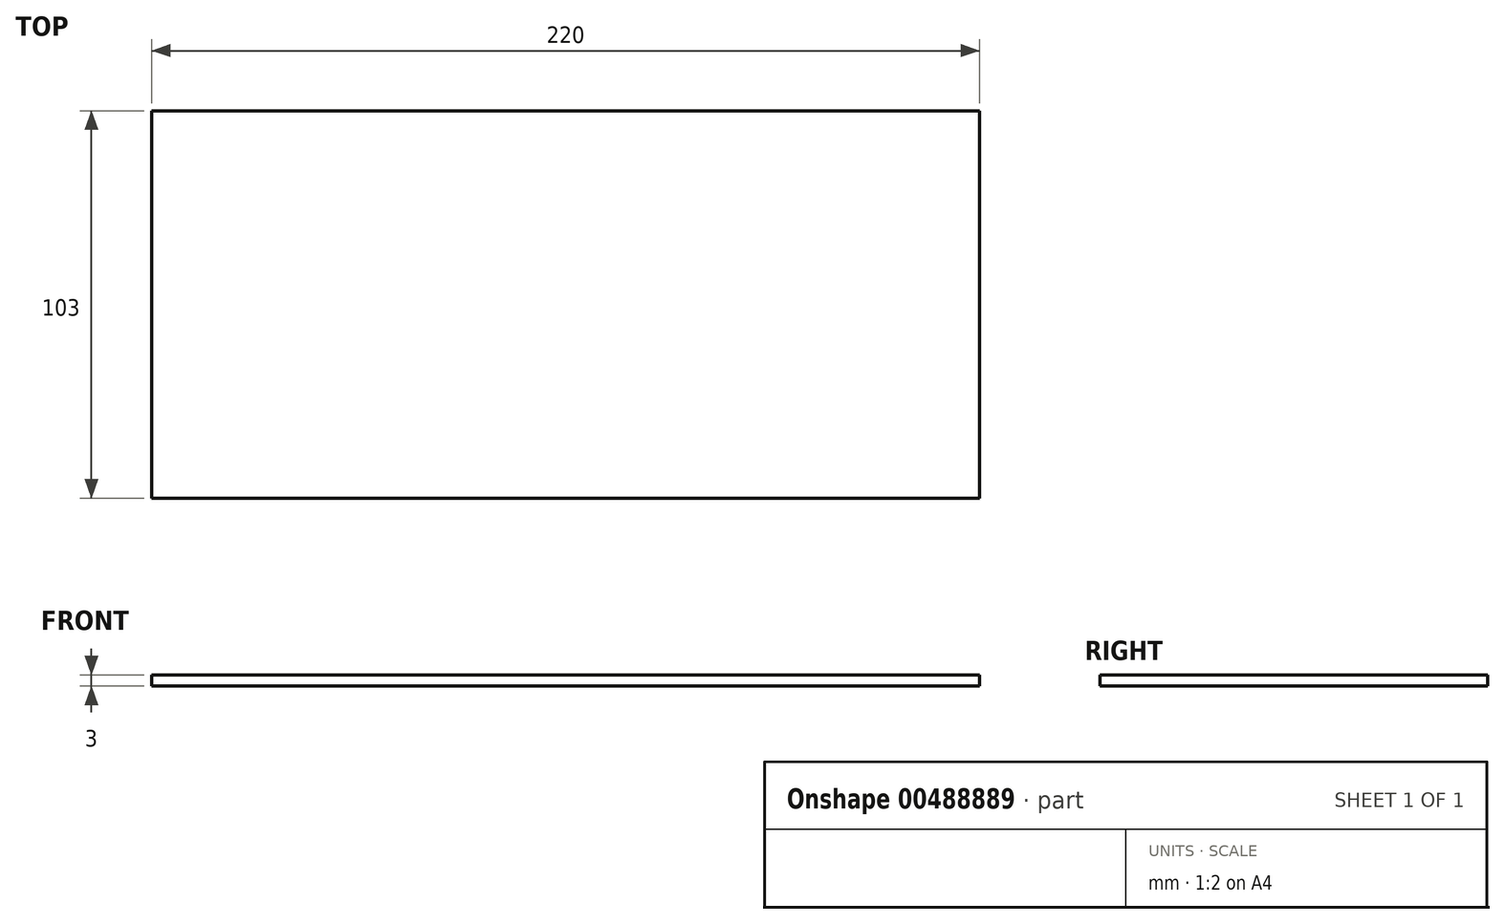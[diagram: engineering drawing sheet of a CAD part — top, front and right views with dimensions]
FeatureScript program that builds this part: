
annotation { "Feature Type Name" : "Feature", "Feature Type Description" : "" }
export const myFeature = defineFeature(function(context is Context, id is Id, definition is map)
    precondition{}
    {
        {
            var Q0;
            Q0=qCreatedBy(makeId("Top.planeOp"),FACE);
            var sketch = newSketch(context, id + "F0", { "sketchPlane" : qUnion([Q0])});
            skLineSegment(sketch, "E0.bottom", {"start": v(-109.4, 80.58) * mm, "end": v(110.6, 80.58) * mm});
            skLineSegment(sketch, "E0.top", {"start": v(-109.4, -22.42) * mm, "end": v(110.6, -22.42) * mm});
            skLineSegment(sketch, "E0.left", {"start": v(-109.4, 80.58) * mm, "end": v(-109.4, -22.42) * mm});
            skLineSegment(sketch, "E0.right", {"start": v(110.6, 80.58) * mm, "end": v(110.6, -22.42) * mm});
            skSolve(sketch);
        }
        {
            var Q0;
            Q0=makeQuery(id+"F0.imprint","IMPRINT",FACE,{"disambiguationData":[TD([[makeQuery(id+"F0.imprint","IMPRINT",EDGE,{"derivedFrom":sQuery(id+"F0.wireOp",EDGE,"E0.bottom")}),-1.0]])]});
            extrude(context, id + "F1", {"entities" : qUnion([Q0]), "depth" : 3 * mm});
        }
    });
